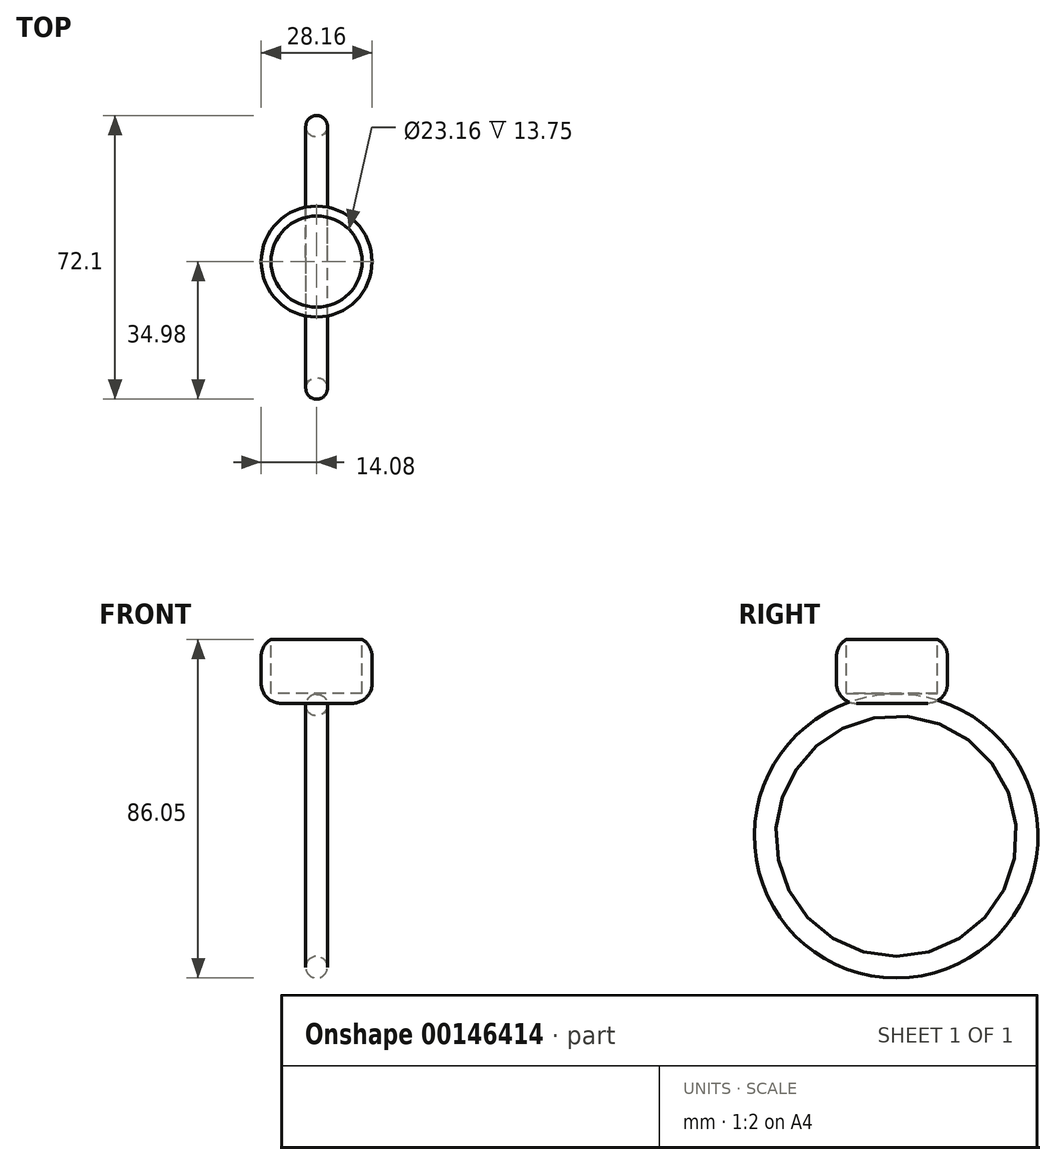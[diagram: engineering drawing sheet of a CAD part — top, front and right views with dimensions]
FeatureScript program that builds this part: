
annotation { "Feature Type Name" : "Feature", "Feature Type Description" : "" }
export const myFeature = defineFeature(function(context is Context, id is Id, definition is map)
    precondition{}
    {
        {
            var Q0;
            Q0=qCreatedBy(makeId("Right.planeOp"),FACE);
            var sketch = newSketch(context, id + "F0", { "sketchPlane" : qUnion([Q0])});
            skCircle(sketch, "E0", {"center": v(0, 0) * mm, "radius": 34.08 * mm});
            skSolve(sketch);
        }
        {
            var Q0;
            Q0=qCreatedBy(makeId("Top.planeOp"),FACE);
            var sketch = newSketch(context, id + "F1", { "sketchPlane" : qUnion([Q0])});
            skCircle(sketch, "E1", {"center": v(0, 33.3) * mm, "radius": 2.75 * mm});
            skSolve(sketch);
        }
        {
            var Q0;
            Q0=makeQuery(id+"F1.imprint","IMPRINT",FACE,{"disambiguationData":[TD([[makeQuery(id+"F1.imprint","IMPRINT",EDGE,{"derivedFrom":sQuery(id+"F1.wireOp",EDGE,"E1")}),1.0]])]});
            var Q1;
            Q1=sQuery(id+"F0.wireOp",EDGE,"E0");
            sweep(context, id + "F2", {"profiles" : qUnion([Q0]), "path" : qUnion([Q1])});
        }
        {
            var Q0;
            Q0=qCreatedBy(makeId("Top.planeOp"),FACE);
            cPlane(context, id + "F3", {"entities" : qUnion([Q0]), "cplaneType" : CPlaneType.OFFSET, "offset" : 50 * mm, "width" : 150 * mm, "height" : 150 * mm});
        }
        {
            var Q0;
            Q0=qCreatedBy(id+"F3.planeOp",FACE);
            var sketch = newSketch(context, id + "F4", { "sketchPlane" : qUnion([Q0])});
            skCircle(sketch, "E2", {"center": v(0, -1.07) * mm, "radius": 14.08 * mm});
            skSolve(sketch);
        }
        {
            var Q0;
            Q0=makeQuery(id+"F4.imprint","IMPRINT",FACE,{"disambiguationData":[TD([[makeQuery(id+"F4.imprint","IMPRINT",EDGE,{"derivedFrom":sQuery(id+"F4.wireOp",EDGE,"E2")}),1.0]])]});
            extrude(context, id + "F5", {"entities" : qUnion([Q0]), "oppositeDirection" : true, "depth" : 16.25 * mm});
        }
        {
            var Q0;
            Q0=makeQuery(id+"F5.opExtrude","CAP_FACE",FACE,{"disambiguationData":[OSD([sQuery(id+"F4.wireOp",EDGE,"E2")])],"isStart":true});
            shell(context, id + "F6", {"entities" : qUnion([Q0]), "thickness" : 2.5 * mm});
        }
        {
            var Q0;
            Q0=makeQuery(id+"F5.opExtrude","CAP_EDGE",EDGE,{"disambiguationData":[OSD([sQuery(id+"F4.wireOp",EDGE,"E2")])],"isStart":true});
            var Q1;
            Q1=makeQuery(id+"F5.opExtrude","CAP_EDGE",EDGE,{"disambiguationData":[OSD([sQuery(id+"F4.wireOp",EDGE,"E2")])],"isStart":false});
            fillet(context, id + "F7", {"entities" : qUnion([Q0, Q1]), "radius" : 5 * mm, "tangentPropagation" : true, "allowEdgeOverflow" : false});
        }
    });
